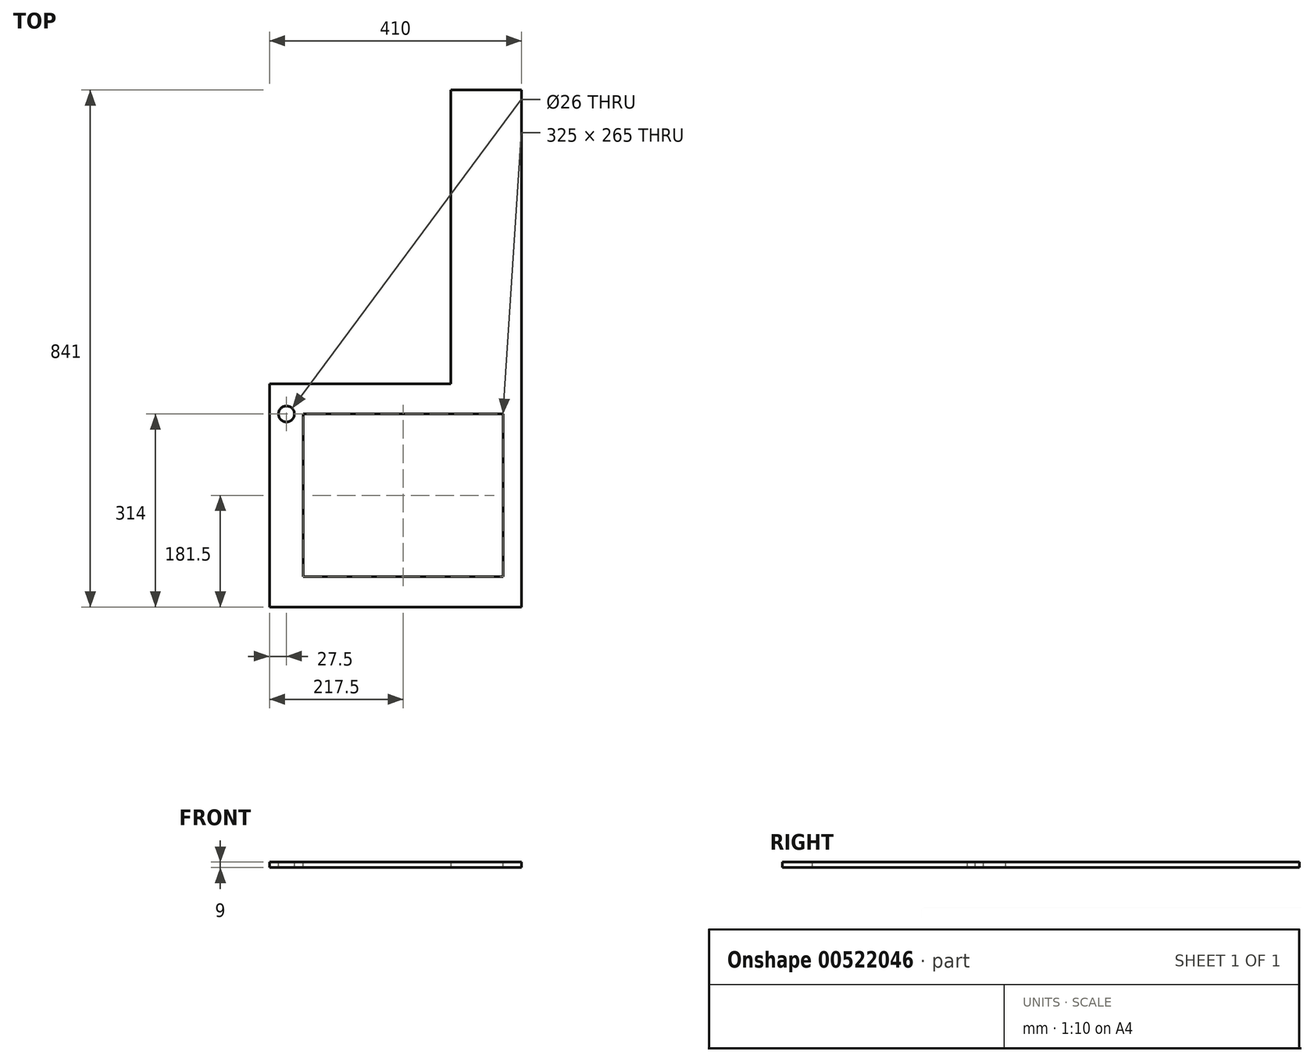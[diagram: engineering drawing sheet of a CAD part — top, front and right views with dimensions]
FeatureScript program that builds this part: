
annotation { "Feature Type Name" : "Feature", "Feature Type Description" : "" }
export const myFeature = defineFeature(function(context is Context, id is Id, definition is map)
    precondition{}
    {
        {
            var Q0;
            Q0=qCreatedBy(makeId("Top.planeOp"),FACE);
            var sketch = newSketch(context, id + "F0", { "sketchPlane" : qUnion([Q0])});
            skLineSegment(sketch, "E0", {"start": v(410, 841) * mm, "end": v(295, 841) * mm});
            skLineSegment(sketch, "E1", {"start": v(0, 363) * mm, "end": v(0, 0) * mm});
            skLineSegment(sketch, "E2", {"start": v(410, 0) * mm, "end": v(0, 0) * mm});
            skLineSegment(sketch, "E3", {"start": v(410, 841) * mm, "end": v(410, 0) * mm});
            skLineSegment(sketch, "E4", {"start": v(0, 363) * mm, "end": v(295, 363) * mm});
            skLineSegment(sketch, "E5", {"start": v(295, 363) * mm, "end": v(295, 841) * mm});
            skSolve(sketch);
        }
        {
            var Q0;
            Q0=makeQuery(id+"F0.imprint","IMPRINT",FACE,{"disambiguationData":[TD([[makeQuery(id+"F0.imprint","IMPRINT",EDGE,{"derivedFrom":sQuery(id+"F0.wireOp",EDGE,"E0")}),1.0]])]});
            extrude(context, id + "F1", {"entities" : qUnion([Q0]), "depth" : 9 * mm, "offsetDistance" : 25 * mm});
        }
        {
            var Q0;
            Q0=makeQuery(id+"F1.opExtrude","CAP_FACE",FACE,{"disambiguationData":[OSD([sQuery(id+"F0.wireOp",EDGE,"E0"),sQuery(id+"F0.wireOp",EDGE,"E1"),sQuery(id+"F0.wireOp",EDGE,"E2"),sQuery(id+"F0.wireOp",EDGE,"E3")])],"isStart":false});
            var sketch = newSketch(context, id + "F2", { "sketchPlane" : qUnion([Q0])});
            skLineSegment(sketch, "E6.bottom", {"start": v(380, 49) * mm, "end": v(55, 49) * mm});
            skLineSegment(sketch, "E6.top", {"start": v(380, 314) * mm, "end": v(55, 314) * mm});
            skLineSegment(sketch, "E6.left", {"start": v(380, 49) * mm, "end": v(380, 314) * mm});
            skLineSegment(sketch, "E6.right", {"start": v(55, 49) * mm, "end": v(55, 314) * mm});
            skCircle(sketch, "E7", {"center": v(27.5, 314) * mm, "radius": 13 * mm});
            skLineSegment(sketch, "E8", {"start": v(55, 314) * mm, "end": v(0, 314) * mm, "construction": true});
            skSolve(sketch);
        }
        {
            var Q0;
            Q0=makeQuery(id+"F2.imprint","IMPRINT",FACE,{"disambiguationData":[TD([[makeQuery(id+"F2.imprint","IMPRINT",EDGE,{"derivedFrom":sQuery(id+"F2.wireOp",EDGE,"E6.bottom")}),-1.0]])]});
            var Q1;
            Q1=makeQuery(id+"F2.imprint","IMPRINT",FACE,{"disambiguationData":[TD([[makeQuery(id+"F2.imprint","IMPRINT",EDGE,{"derivedFrom":sQuery(id+"F2.wireOp",EDGE,"E7")}),1.0]])]});
            extrude(context, id + "F3", {"entities" : qUnion([Q0, Q1]), "operationType" : NewBodyOperationType.REMOVE, "oppositeDirection" : true, "depth" : 25 * mm, "offsetDistance" : 25 * mm});
        }
    });
